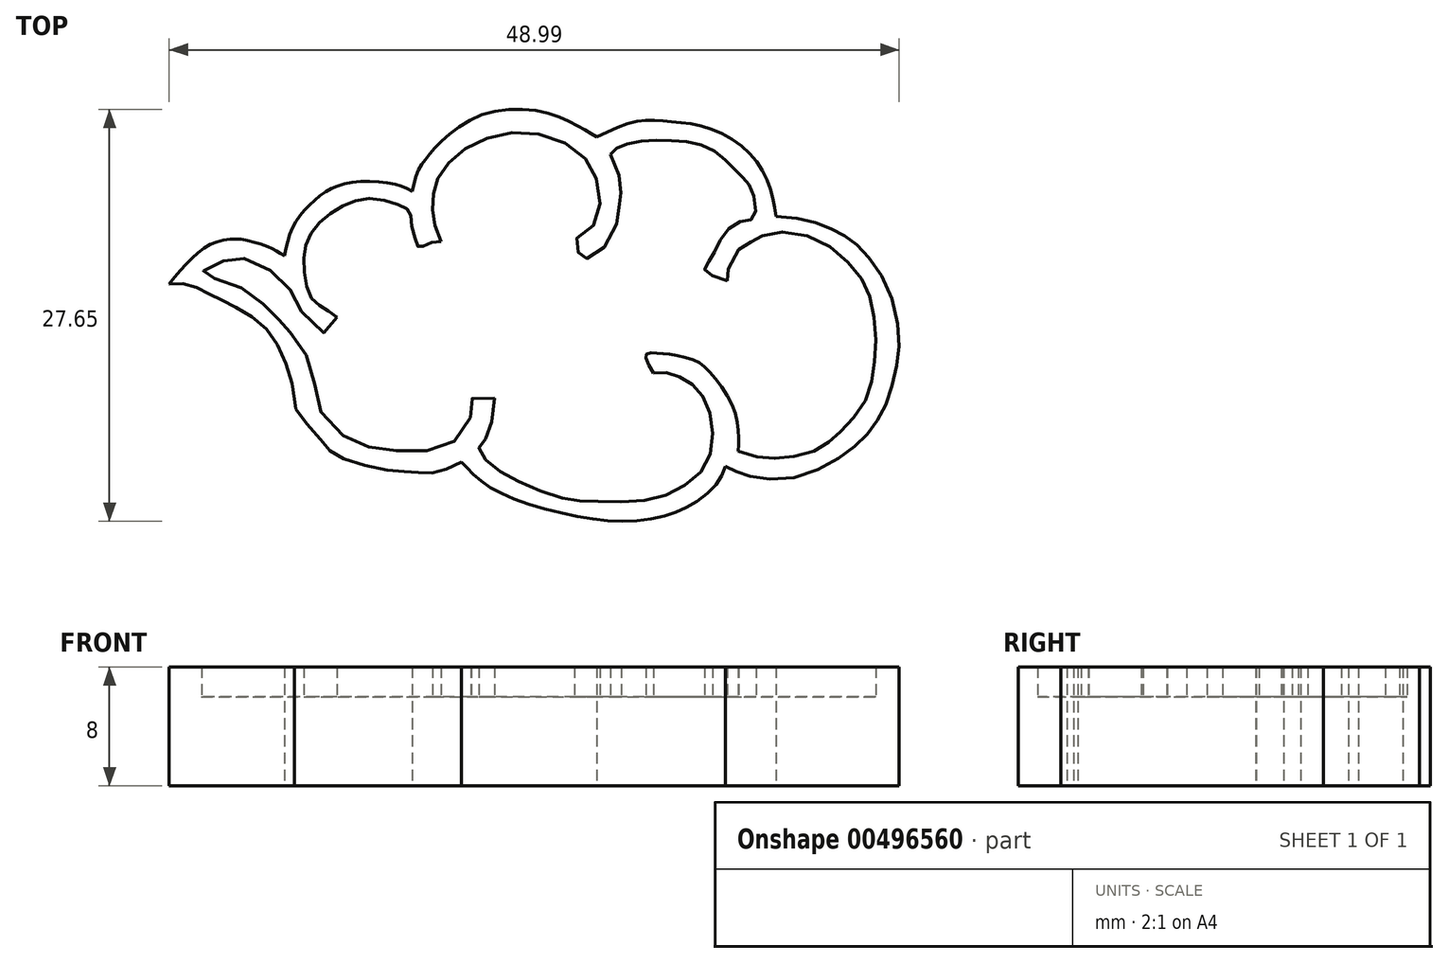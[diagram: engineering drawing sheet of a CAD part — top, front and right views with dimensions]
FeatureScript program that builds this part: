
annotation { "Feature Type Name" : "Feature", "Feature Type Description" : "" }
export const myFeature = defineFeature(function(context is Context, id is Id, definition is map)
    precondition{}
    {
        {
            var Q0;
            Q0=qCreatedBy(makeId("Top.planeOp"),FACE);
            var sketch = newSketch(context, id + "F0", { "sketchPlane" : qUnion([Q0])});
            skFitSpline(sketch, "E0", {"points": [v(5.7, 32.07) * mm, v(7.05, 32.02) * mm, v(8.45, 31.37) * mm, v(9.81, 30.7) * mm, v(11.9, 29.38) * mm, v(13.39, 27.08) * mm, v(14.09, 24.49) * mm, v(14.19, 23.74) * mm, v(15.89, 21.6) * mm, v(16.98, 20.54) * mm, v(20.33, 19.6) * mm, v(22.17, 19.45) * mm, v(23.57, 19.45) * mm, v(25.32, 20.14) * mm], "startDerivative": vector(21.41, 1.49) * mm, "endDerivative": vector(23.47, 11.78) * mm});
            skFitSpline(sketch, "E1", {"points": [v(25.32, 20.14) * mm, v(25.97, 19.45) * mm, v(27.16, 18.5) * mm, v(29.4, 17.45) * mm, v(33.05, 16.5) * mm, v(36.15, 16.15) * mm, v(38.84, 16.5) * mm, v(40.64, 17.2) * mm, v(42.33, 18.55) * mm, v(43.03, 19.85) * mm], "startDerivative": vector(8.08, -9.24) * mm, "endDerivative": vector(5.8, 14.3) * mm});
            skFitSpline(sketch, "E2", {"points": [v(43.03, 19.85) * mm, v(43.73, 19.5) * mm, v(44.88, 19.15) * mm, v(47.62, 19.1) * mm, v(50.57, 20.34) * mm, v(52.17, 21.6) * mm, v(53.16, 22.84) * mm, v(53.96, 24.44) * mm, v(54.51, 26.63) * mm, v(54.66, 28.88) * mm, v(53.71, 32.27) * mm, v(52.27, 34.27) * mm, v(51.27, 35.17) * mm, v(50.12, 35.76) * mm, v(48.67, 36.31) * mm, v(46.43, 36.61) * mm], "startDerivative": vector(15.9, -8.57) * mm, "endDerivative": vector(-33.08, 2.75) * mm});
            skFitSpline(sketch, "E3", {"points": [v(46.43, 36.61) * mm, v(45.93, 38.8) * mm, v(44.33, 41.15) * mm, v(41.49, 42.65) * mm, v(39.04, 43) * mm, v(37.14, 43) * mm, v(34.4, 41.95) * mm], "startDerivative": vector(-2.1, 14.03) * mm, "endDerivative": vector(-16.17, -7.55) * mm});
            skFitSpline(sketch, "E4", {"points": [v(34.4, 41.95) * mm, v(33.35, 42.55) * mm, v(30.86, 43.6) * mm, v(26.61, 43.4) * mm, v(23.82, 41.5) * mm, v(22.87, 40.4) * mm, v(22.37, 39.6) * mm, v(22.02, 38.3) * mm], "startDerivative": vector(-8.63, 5) * mm, "endDerivative": vector(-2.5, -12.03) * mm});
            skFitSpline(sketch, "E5", {"points": [v(22.02, 38.3) * mm, v(20.68, 38.8) * mm, v(17.98, 38.9) * mm, v(16.28, 38.3) * mm, v(14.99, 37.26) * mm, v(13.94, 35.76) * mm, v(13.44, 33.97) * mm], "startDerivative": vector(-8.06, 3.85) * mm, "endDerivative": vector(-2.2, -11.1) * mm});
            skFitSpline(sketch, "E6", {"points": [v(13.44, 33.97) * mm, v(12.34, 34.57) * mm, v(11.44, 34.87) * mm, v(10.6, 35.07) * mm, v(8.45, 34.72) * mm, v(5.7, 32.07) * mm], "startDerivative": vector(-6.38, 3.85) * mm, "endDerivative": vector(-8.62, -10.67) * mm});
            skFitSpline(sketch, "E7", {"points": [v(16.95, 29.84) * mm, v(16.05, 30.5) * mm, v(15.2, 31.2) * mm, v(14.75, 33.04) * mm, v(14.9, 34.78) * mm, v(15.85, 36.28) * mm, v(17.5, 37.38) * mm, v(19.4, 37.83) * mm, v(21.34, 37.28) * mm, v(21.84, 36.93) * mm, v(21.99, 35.93) * mm, v(22.34, 34.73) * mm, v(22.49, 34.53) * mm, v(23.09, 34.78) * mm, v(23.93, 34.93) * mm], "startDerivative": vector(-13.02, 10) * mm, "endDerivative": vector(14.17, 2.03) * mm});
            skFitSpline(sketch, "E8", {"points": [v(23.93, 34.93) * mm, v(23.48, 36.13) * mm, v(23.38, 37.28) * mm, v(23.48, 38.38) * mm, v(23.93, 39.52) * mm, v(25.23, 40.92) * mm, v(27.53, 42.02) * mm, v(30.62, 42.12) * mm, v(33.47, 40.67) * mm, v(34.51, 38.53) * mm, v(34.21, 36.03) * mm, v(32.92, 34.93) * mm, v(33.32, 33.99) * mm, v(33.62, 33.79) * mm, v(35.21, 34.93) * mm, v(35.91, 37.28) * mm, v(35.96, 37.83) * mm, v(36.01, 38.83) * mm, v(35.31, 40.77) * mm], "startDerivative": vector(-11.03, 23.52) * mm, "endDerivative": vector(-15.06, 32.82) * mm});
            skFitSpline(sketch, "E9", {"points": [v(35.31, 40.77) * mm, v(35.86, 41.27) * mm, v(37.56, 41.67) * mm, v(39.8, 41.67) * mm, v(41.9, 41.22) * mm, v(43.4, 40.02) * mm, v(44.3, 39.13) * mm, v(44.84, 38.28) * mm, v(44.94, 36.53) * mm, v(43.9, 36.23) * mm, v(42.65, 34.93) * mm, v(42, 33.69) * mm, v(41.65, 32.99) * mm, v(43.15, 32.29) * mm], "startDerivative": vector(8.02, 9.81) * mm, "endDerivative": vector(24.9, -8.02) * mm});
            skFitSpline(sketch, "E10", {"points": [v(43.15, 32.29) * mm, v(43.15, 32.84) * mm, v(44.1, 34.58) * mm, v(44.84, 34.93) * mm, v(45.64, 35.38) * mm, v(48.14, 35.43) * mm, v(50.73, 34.04) * mm, v(52.23, 32.29) * mm, v(52.88, 30.6) * mm, v(53.13, 28.2) * mm, v(52.93, 26.05) * mm, v(52.43, 24.25) * mm, v(51.18, 22.6) * mm, v(50.18, 21.66) * mm, v(49.09, 20.91) * mm, v(47.19, 20.46) * mm, v(45.6, 20.41) * mm, v(43.9, 20.86) * mm], "startDerivative": vector(-3.99, 18.04) * mm, "endDerivative": vector(-32.02, 9.1) * mm});
            skFitSpline(sketch, "E11", {"points": [v(43.9, 20.86) * mm, v(43.9, 22.1) * mm, v(43.45, 24.05) * mm, v(42, 26.15) * mm, v(41, 26.95) * mm, v(39.35, 27.35) * mm, v(38.3, 27.45) * mm, v(37.7, 27.35) * mm, v(38.2, 26.1) * mm], "startDerivative": vector(0.35, 10.1) * mm, "endDerivative": vector(7.57, -12.95) * mm});
            skFitSpline(sketch, "E12", {"points": [v(38.2, 26.1) * mm, v(39.2, 26.1) * mm, v(40.35, 25.65) * mm, v(41.4, 24.7) * mm, v(42.1, 22.8) * mm, v(41.85, 20.21) * mm, v(40.05, 18.41) * mm, v(37.3, 17.52) * mm, v(34.16, 17.52) * mm, v(32.27, 17.67) * mm, v(29.27, 18.76) * mm, v(27.18, 20.06) * mm, v(26.48, 21.1) * mm, v(26.98, 21.76) * mm, v(27.53, 24.4) * mm], "startDerivative": vector(19.5, 1.67) * mm, "endDerivative": vector(3.51, 38.2) * mm});
            skFitSpline(sketch, "E13", {"points": [v(27.53, 24.4) * mm, v(26.03, 24.4) * mm, v(25.98, 23.56) * mm, v(24.93, 21.6) * mm, v(22.54, 20.86) * mm, v(19.9, 21) * mm, v(17.85, 21.6) * mm, v(15.75, 23.75) * mm, v(15.35, 26.1) * mm, v(14.1, 28.5) * mm, v(13.3, 29.38) * mm, v(12.8, 30) * mm, v(11.36, 31.24) * mm, v(9.41, 32.29) * mm, v(7.86, 32.74) * mm, v(8.66, 33.34) * mm, v(9.91, 33.79) * mm, v(11.46, 33.59) * mm, v(13.65, 31.94) * mm, v(14.3, 30.7) * mm, v(16.15, 28.8) * mm, v(16.95, 29.84) * mm], "startDerivative": vector(-45.45, 6.8) * mm, "endDerivative": vector(14.13, 38.6) * mm});
            skSolve(sketch);
        }
        {
            var Q0;
            Q0=makeQuery(id+"F0.imprint","IMPRINT",FACE,{"disambiguationData":[TD([[makeQuery(id+"F0.imprint","IMPRINT",EDGE,{"derivedFrom":sQuery(id+"F0.wireOp",EDGE,"E0")}),1.0]])]});
            extrude(context, id + "F1", {"entities" : qUnion([Q0]), "depth" : 8 * mm, "offsetDistance" : 25 * mm});
        }
        {
            var Q0;
            Q0 = qSketchRegion(id + "F0", true);
            var Q1;
            Q1=makeQuery(id+"F0.imprint","IMPRINT",FACE,{"disambiguationData":[TD([[makeQuery(id+"F0.imprint","IMPRINT",EDGE,{"derivedFrom":sQuery(id+"F0.wireOp",EDGE,"E7")}),-1.0]])]});
            extrude(context, id + "F2", {"entities" : qUnion([Q0, Q1]), "operationType" : NewBodyOperationType.ADD, "depth" : 6 * mm, "offsetDistance" : 25 * mm});
        }
    });
